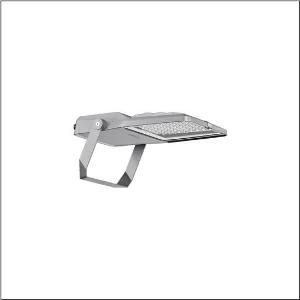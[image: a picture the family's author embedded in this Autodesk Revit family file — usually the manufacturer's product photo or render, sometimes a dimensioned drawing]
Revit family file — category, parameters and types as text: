
# Revit family: floodlight_fl_21_iq_mini___pl33t_5xa7772d3f1a_bc4e
name_source: partatom
category: Lighting Fixtures
units: mm (PartAtom-declared; Revit-internal decimal feet)

## family parameters
Cut with Voids When Loaded = No
Host = Face
Light Source = No
Part Type = Normal
Room Calculation Point = No
Round Connector Dimension = Use Diameter
Shared = No

## types (1)
- --- (1 x LED, 15160 lm, 143 W, 3000K)
    Apparent Load = 143 VA
    CIE Flux Codes = 26 75 99 100 100
    Color Rendering = 80
    Color Temperature = 3000K
    Default Elevation = 1800 mm
    Description = Floodlight FL 21 iQ mini, floodlight, primary light control with lens, of PMMA, primary optical cover: protective disc, of toughened safety glass, transparent, light distribution: PL33T, light emission: direct distribution, installation type: surface-mounted, LED, High Power LED, rated luminous flux: 15.160lm, luminous efficacy: 106lm/W, light colour: 830, colour temperature: 3000K, control: Street-Remote, Auto-Match, Temp-Guard, Night-Set, Smart-Wire, Desk-Remote (wireless, voltage-free reading and setting of iQ features in the workshop via application-optimized NFC function/RFID function), optimised constant luminous flux control (CLO 2.0), with terminal, 6-pole, mains connection: 220..240V, AC, 50/60Hz, start of lifetime: 143W, end of service life: 152W, reduction: 61W, luminaire housing, of diecast aluminium, powder-coated, Siteco® metallic grey (DB 702S), corrosivity category C5 mid according to DIN EN ISO 12944, sealing non-destructively replaceable, mounting bracket, of steel, galvanised, powder-coated, Siteco® metallic grey (DB 702S), protection rating (complete): IP66, insulation class (complete): insulation class II (safety insulation), certification: CE, ENEC, VDE, protection symbol: D, impact resistance: IK08, permissible operating ambient temperature: -40..+40°C, permissible operating ambient temperature for outdoor applications: -40..+50°C, standard: DIN EN 12944, LABS conformity tested according to VDMA 24364:2018-05, packaging unit: 1 piece

Light Distribution: PL33T
    Height = 70 mm
    Lamp = 1 x LED
    Lamp Light Flux = 15160 lm
    Lamp Power = 143 W
    Lamp count = 1
    Length = 485 mm
    Luminous efficacy = 106 lm/W
    Manufacturer = Siteco
    ModVariant = No
    Model = 5XA7772D3F1A
    Number of Poles = 1
    OnlyDefault = Yes
    Power Factor = 1
    Product Name = Floodlight FL 21 iQ mini | PL33T
    Product group = floodlight | pylon annexe
    ProductGroupID = 6200
    Protection Class = Protection class II
    Protection Degree = IP 66
    RLX_Detail_Level = 1
    RLX_Emergency_Light_Flux = 0 lm
    RLX_Emergency_Type = 0
    RLX_Emergency_Type_DB = No
    RlxData = <blob elided: 96345 chars, md5=9e6b4f03>
    Socket = socket
    Standby Power = 0 W
    System Light Flux = 15160 lm
    System Power = 143 W
    Type Comments = factory setting: luminous flux: 100 % | dim-lin: 254 | 730 mA
    Type Image = l_1006845.jpg
    URL = http://relux.com
    VarID = @adj_081377
    Voltage = 0 V
    Weight = 0.00 kg
    Width = 337 mm

## geometry (parser evidence)
native form markers: Blend x4, Sweep x12
no freeform markers — native parametric forms only
